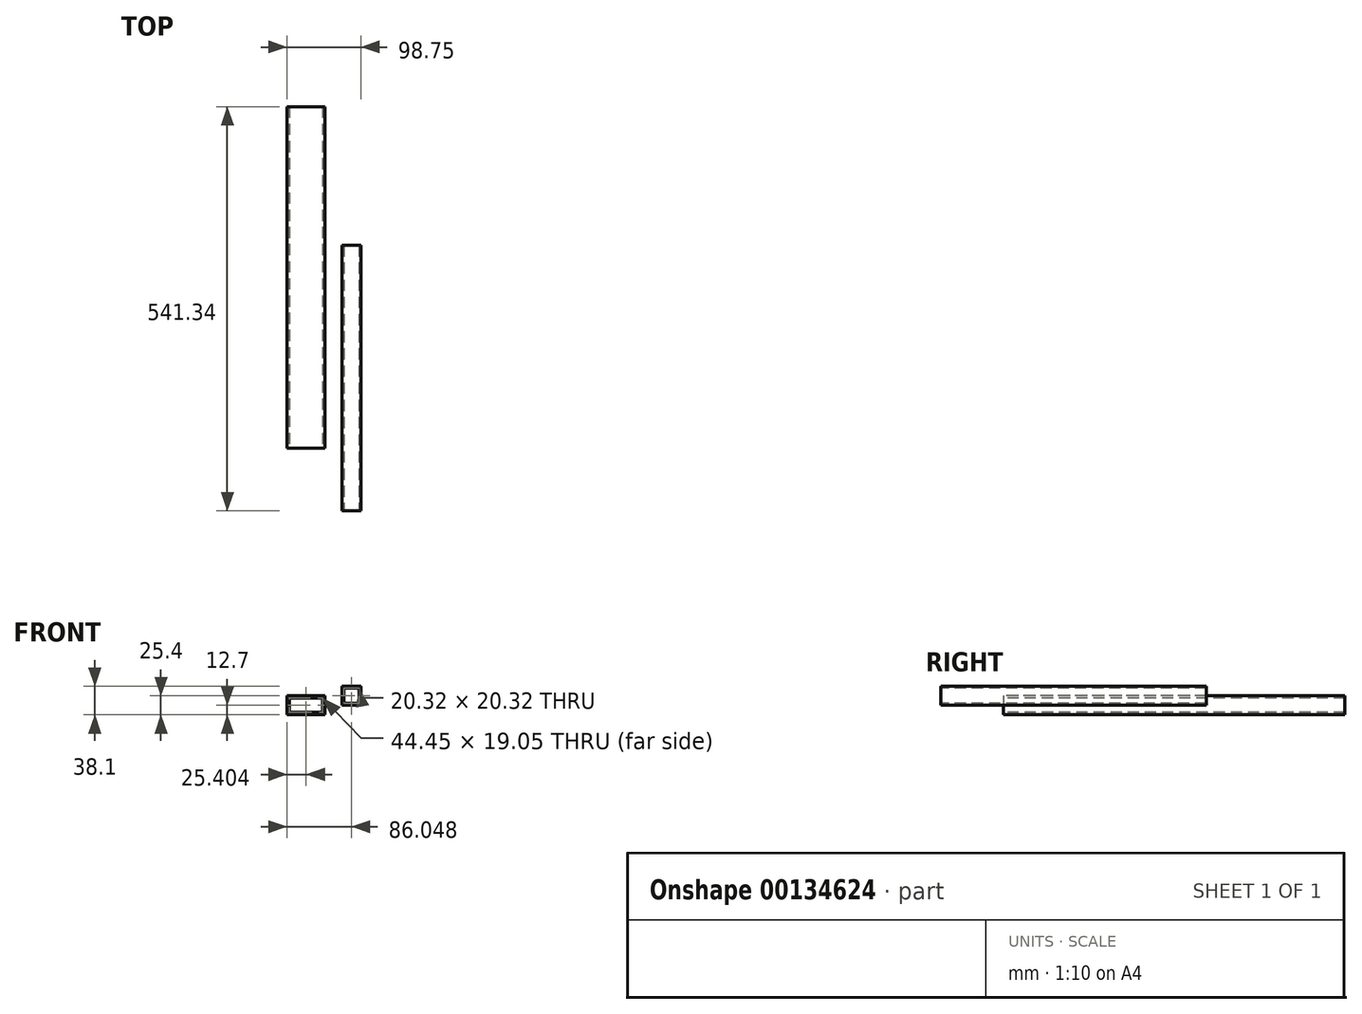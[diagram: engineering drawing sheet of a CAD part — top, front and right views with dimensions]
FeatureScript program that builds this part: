
annotation { "Feature Type Name" : "Feature", "Feature Type Description" : "" }
export const myFeature = defineFeature(function(context is Context, id is Id, definition is map)
    precondition{}
    {
        {
            var Q0;
            Q0=qCreatedBy(makeId("Top.planeOp"),FACE);
            var sketch = newSketch(context, id + "F0", { "sketchPlane" : qUnion([Q0])});
            skLineSegment(sketch, "E0.bottom", {"start": v(-70.48, 379.43) * mm, "end": v(-19.68, 379.43) * mm});
            skLineSegment(sketch, "E0.top", {"start": v(-70.48, -77.77) * mm, "end": v(-19.68, -77.77) * mm});
            skLineSegment(sketch, "E0.left", {"start": v(-70.48, 379.43) * mm, "end": v(-70.48, -77.77) * mm});
            skLineSegment(sketch, "E0.right", {"start": v(-19.68, 379.43) * mm, "end": v(-19.68, -77.77) * mm});
            skSolve(sketch);
        }
        {
            var Q0;
            Q0=makeQuery(id+"F0.imprint","IMPRINT",FACE,{"disambiguationData":[TD([[makeQuery(id+"F0.imprint","IMPRINT",EDGE,{"derivedFrom":sQuery(id+"F0.wireOp",EDGE,"E0.bottom")}),-1.0]])]});
            extrude(context, id + "F1", {"entities" : qUnion([Q0]), "endBound" : BoundingType.SYMMETRIC, "depth" : 25.4 * mm});
        }
        {
            var Q0;
            Q0=makeQuery(id+"F1.opExtrude","SWEPT_FACE",FACE,{"disambiguationData":[OSD([sQuery(id+"F0.wireOp",EDGE,"E0.bottom")])]});
            var Q1;
            Q1=makeQuery(id+"F1.opExtrude","SWEPT_FACE",FACE,{"disambiguationData":[OSD([sQuery(id+"F0.wireOp",EDGE,"E0.top")])]});
            shell(context, id + "F2", {"entities" : qUnion([Q0, Q1]), "thickness" : 3.17 * mm});
        }
        {
            var Q0;
            Q0=qCreatedBy(makeId("Top.planeOp"),FACE);
            var sketch = newSketch(context, id + "F3", { "sketchPlane" : qUnion([Q0])});
            skLineSegment(sketch, "E1.bottom", {"start": v(2.87, 193.69) * mm, "end": v(28.27, 193.69) * mm});
            skLineSegment(sketch, "E1.top", {"start": v(2.87, -161.91) * mm, "end": v(28.27, -161.91) * mm});
            skLineSegment(sketch, "E1.left", {"start": v(2.87, 193.69) * mm, "end": v(2.87, -161.91) * mm});
            skLineSegment(sketch, "E1.right", {"start": v(28.27, 193.69) * mm, "end": v(28.27, -161.91) * mm});
            skSolve(sketch);
        }
        {
            var Q0;
            Q0=makeQuery(id+"F3.imprint","IMPRINT",FACE,{"disambiguationData":[TD([[makeQuery(id+"F3.imprint","IMPRINT",EDGE,{"derivedFrom":sQuery(id+"F3.wireOp",EDGE,"E1.bottom")}),-1.0]])]});
            extrude(context, id + "F4", {"entities" : qUnion([Q0]), "depth" : 25.4 * mm});
        }
        {
            var Q0;
            Q0=makeQuery(id+"F4.opExtrude","SWEPT_FACE",FACE,{"disambiguationData":[OSD([sQuery(id+"F3.wireOp",EDGE,"E1.bottom")])]});
            var Q1;
            Q1=makeQuery(id+"F4.opExtrude","SWEPT_FACE",FACE,{"disambiguationData":[OSD([sQuery(id+"F3.wireOp",EDGE,"E1.top")])]});
            shell(context, id + "F5", {"entities" : qUnion([Q0, Q1]), "thickness" : 2.54 * mm});
        }
    });
